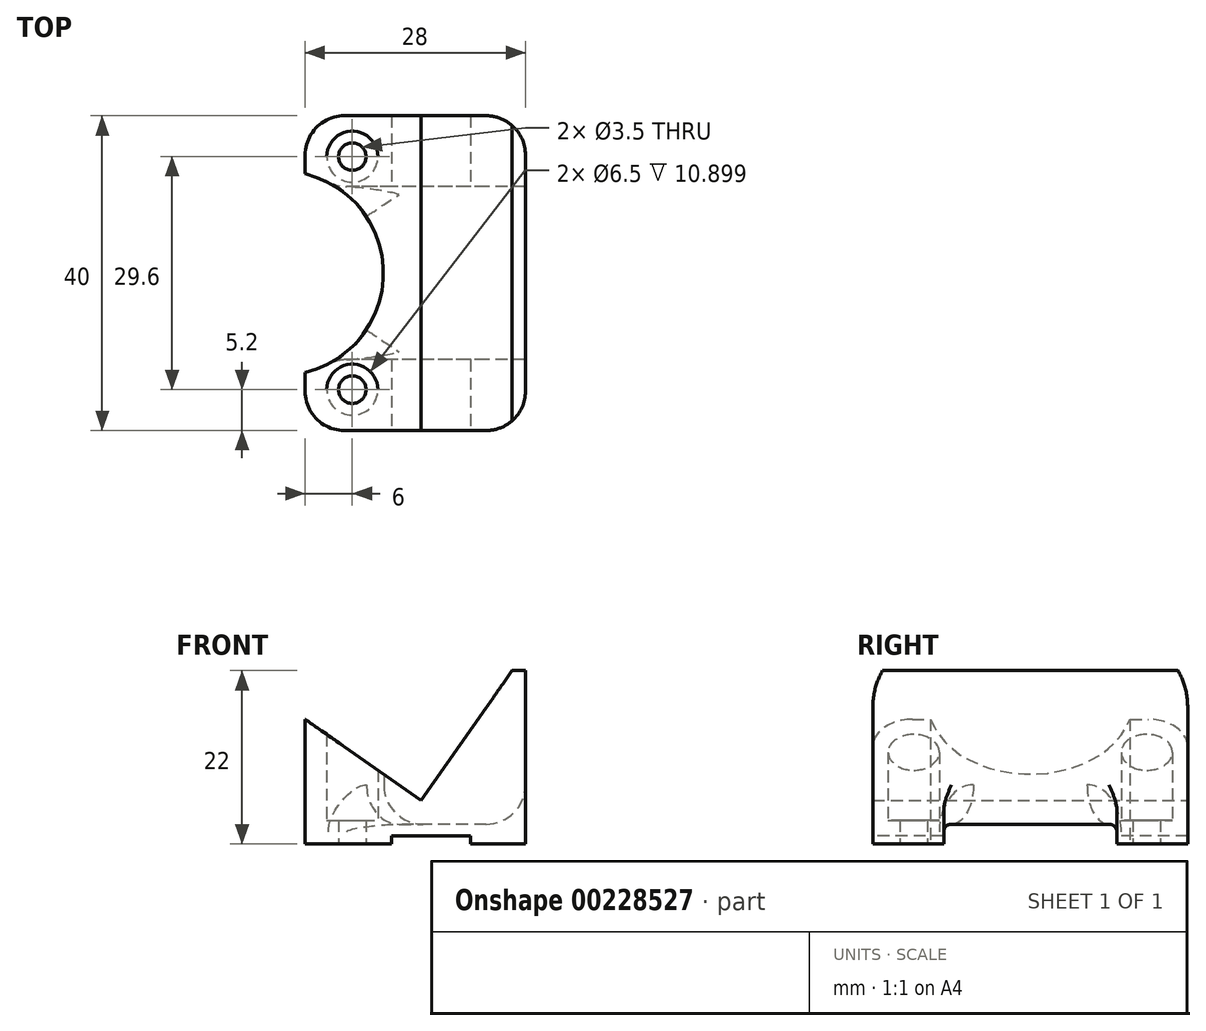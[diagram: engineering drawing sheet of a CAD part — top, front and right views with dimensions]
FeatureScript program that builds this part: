
annotation { "Feature Type Name" : "Feature", "Feature Type Description" : "" }
export const myFeature = defineFeature(function(context is Context, id is Id, definition is map)
    precondition{}
    {
        {
            var Q0;
            Q0=qCreatedBy(makeId("Front.planeOp"),FACE);
            var sketch = newSketch(context, id + "F0", { "sketchPlane" : qUnion([Q0])});
            skLineSegment(sketch, "E0.bottom", {"start": v(0, 0) * mm, "end": v(28, 0) * mm});
            skLineSegment(sketch, "E0.top", {"start": v(26.3, 22) * mm, "end": v(28, 22) * mm});
            skLineSegment(sketch, "E0.left", {"start": v(0, 0) * mm, "end": v(0, 15.82) * mm});
            skLineSegment(sketch, "E0.right", {"start": v(28, 0) * mm, "end": v(28, 22) * mm});
            skLineSegment(sketch, "E1", {"start": v(0, 15.82) * mm, "end": v(14.74, 5.5) * mm});
            skLineSegment(sketch, "E2", {"start": v(14.74, 5.5) * mm, "end": v(26.3, 22) * mm});
            skSolve(sketch);
        }
        {
            var Q0;
            Q0=qSketchRegion(id+"F0",true);
            extrude(context, id + "F1", {"entities" : qUnion([Q0]), "endBound" : BoundingType.SYMMETRIC, "depth" : 40 * mm});
        }
        {
            var Q0;
            Q0=makeQuery(id+"F1.opExtrude","SWEPT_FACE",FACE,{"disambiguationData":[OSD([sQuery(id+"F0.wireOp",EDGE,"E0.bottom")])]});
            var sketch = newSketch(context, id + "F2", { "sketchPlane" : qUnion([Q0])});
            skCircle(sketch, "E3", {"center": v(6, 14.8) * mm, "radius": 1.75 * mm});
            skCircle(sketch, "E4", {"center": v(6, -14.8) * mm, "radius": 1.75 * mm});
            skCircle(sketch, "E5", {"center": v(-3, 0) * mm, "radius": 13 * mm});
            skSolve(sketch);
        }
        {
            var Q0;
            Q0=qSketchRegion(id+"F2",true);
            extrude(context, id + "F3", {"entities" : qUnion([Q0]), "operationType" : NewBodyOperationType.REMOVE, "endBound" : BoundingType.THROUGH_ALL, "oppositeDirection" : true, "depth" : 25 * mm});
        }
        {
            var Q0;
            Q0=makeQuery(id+"F1.opExtrude","SWEPT_FACE",FACE,{"disambiguationData":[OSD([sQuery(id+"F0.wireOp",EDGE,"E0.left")])]});
            var sketch = newSketch(context, id + "F4", { "sketchPlane" : qUnion([Q0])});
            skLineSegment(sketch, "E6.bottom", {"start": v(-11, 2.5) * mm, "end": v(11, 2.5) * mm});
            skLineSegment(sketch, "E6.top", {"start": v(-11, 0) * mm, "end": v(11, 0) * mm});
            skLineSegment(sketch, "E6.left", {"start": v(-11, 2.5) * mm, "end": v(-11, 0) * mm});
            skLineSegment(sketch, "E6.right", {"start": v(11, 2.5) * mm, "end": v(11, 0) * mm});
            skSolve(sketch);
        }
        {
            var Q0;
            Q0=qSketchRegion(id+"F4",true);
            extrude(context, id + "F5", {"entities" : qUnion([Q0]), "operationType" : NewBodyOperationType.REMOVE, "endBound" : BoundingType.THROUGH_ALL, "oppositeDirection" : true, "depth" : 25 * mm});
        }
        {
            var Q0;
            Q0=makeQuery(id+"F5.boolean.opBoolean","INTERSECT",EDGE,{"derivedFrom":[makeQuery(id+"F1.opExtrude","SWEPT_FACE",FACE,{"disambiguationData":[OSD([sQuery(id+"F0.wireOp",EDGE,"E0.right")])]}),makeQuery(id+"F5.opExtrude","SWEPT_FACE",FACE,{"disambiguationData":[OSD([sQuery(id+"F4.wireOp",EDGE,"E6.bottom")])]})]});
            fillet(context, id + "F6", {"entities" : qUnion([Q0]), "radius" : 5 * mm, "tangentPropagation" : true, "allowEdgeOverflow" : false});
        }
        {
            var Q0;
            Q0=makeQuery(id+"F1.opExtrude","CAP_EDGE",EDGE,{"disambiguationData":[OSD([sQuery(id+"F0.wireOp",EDGE,"E0.left")])],"isStart":false});
            var Q1;
            Q1=makeQuery(id+"F1.opExtrude","CAP_EDGE",EDGE,{"disambiguationData":[OSD([sQuery(id+"F0.wireOp",EDGE,"E0.left")])],"isStart":true});
            fillet(context, id + "F7", {"entities" : qUnion([Q0, Q1]), "radius" : 5 * mm, "tangentPropagation" : true, "allowEdgeOverflow" : false});
        }
        {
            var Q0;
            Q0=makeQuery(id+"F5.boolean.opBoolean","COPY",EDGE,{"derivedFrom":makeQuery(id+"F5.opExtrude","SWEPT_EDGE",EDGE,{"disambiguationData":[OSD([sQuery(id+"F4.wireOp",EDGE,"E6.bottom"),sQuery(id+"F4.wireOp",EDGE,"E6.left")])]})});
            var Q1;
            Q1=makeQuery(id+"F5.boolean.opBoolean","COPY",EDGE,{"derivedFrom":makeQuery(id+"F5.opExtrude","SWEPT_EDGE",EDGE,{"disambiguationData":[OSD([sQuery(id+"F4.wireOp",EDGE,"E6.bottom"),sQuery(id+"F4.wireOp",EDGE,"E6.right")])]})});
            fillet(context, id + "F8", {"entities" : qUnion([Q0, Q1]), "radius" : 1 * mm, "tangentPropagation" : true, "allowEdgeOverflow" : false});
        }
        {
            var Q0;
            Q0=makeQuery(id+"F1.opExtrude","CAP_EDGE",EDGE,{"disambiguationData":[OSD([sQuery(id+"F0.wireOp",EDGE,"E0.right")])],"isStart":true});
            var Q1;
            Q1=makeQuery(id+"F1.opExtrude","CAP_EDGE",EDGE,{"disambiguationData":[OSD([sQuery(id+"F0.wireOp",EDGE,"E0.right")])],"isStart":false});
            fillet(context, id + "F9", {"entities" : qUnion([Q0, Q1]), "radius" : 5 * mm, "tangentPropagation" : true, "allowEdgeOverflow" : false});
        }
        {
            var Q0;
            {var subQ2=sQuery(id+"F0.wireOp",EDGE,"E0.bottom");Q0=makeQuery(id+"F5.boolean.opBoolean","SPLIT",FACE,{"disambiguationData":[TD([makeQuery(id+"F3.boolean.opBoolean","COPY",FACE,{"derivedFrom":makeQuery(id+"F3.opExtrude","SWEPT_FACE",FACE,{"disambiguationData":[OSD([sQuery(id+"F2.wireOp",EDGE,"E4")])]})})])],"derivedFrom":makeQuery(id+"F1.opExtrude","SWEPT_FACE",FACE,{"disambiguationData":[OSD([subQ2])]})});}
            var sketch = newSketch(context, id + "F10", { "sketchPlane" : qUnion([Q0])});
            skCircle(sketch, "E7", {"center": v(6, 14.8) * mm, "radius": 3.25 * mm});
            skCircle(sketch, "E8", {"center": v(6, -14.8) * mm, "radius": 3.25 * mm});
            skSolve(sketch);
        }
        {
            var Q0;
            Q0=qSketchRegion(id+"F10",true);
            extrude(context, id + "F11", {"entities" : qUnion([Q0]), "operationType" : NewBodyOperationType.REMOVE, "oppositeDirection" : true, "depth" : 25 * mm, "hasSecondDirection" : true, "secondDirectionOppositeDirection" : true, "secondDirectionDepth" : 3 * mm});
        }
        {
            var Q0;
            Q0=makeQuery(id+"F5.boolean.opBoolean","INTERSECT",EDGE,{"derivedFrom":[makeQuery(id+"F3.boolean.opBoolean","COPY",FACE,{"derivedFrom":makeQuery(id+"F3.opExtrude","SWEPT_FACE",FACE,{"disambiguationData":[OSD([sQuery(id+"F2.wireOp",EDGE,"E5")])]})}),makeQuery(id+"F5.opExtrude","SWEPT_FACE",FACE,{"disambiguationData":[OSD([sQuery(id+"F4.wireOp",EDGE,"E6.bottom")])]})]});
            fillet(context, id + "F12", {"entities" : qUnion([Q0]), "radius" : 5 * mm, "tangentPropagation" : true, "allowEdgeOverflow" : false});
        }
        {
            var Q0;
            Q0=makeQuery(id+"F1.opExtrude","CAP_FACE",FACE,{"disambiguationData":[OSD([sQuery(id+"F0.wireOp",EDGE,"E0.bottom"),sQuery(id+"F0.wireOp",EDGE,"E0.top"),sQuery(id+"F0.wireOp",EDGE,"E0.left"),sQuery(id+"F0.wireOp",EDGE,"E0.right"),sQuery(id+"F0.wireOp",EDGE,"E1"),sQuery(id+"F0.wireOp",EDGE,"E2")])],"isStart":false});
            var sketch = newSketch(context, id + "F13", { "sketchPlane" : qUnion([Q0])});
            skLineSegment(sketch, "E9.bottom", {"start": v(11, 0) * mm, "end": v(21, 0) * mm});
            skLineSegment(sketch, "E9.top", {"start": v(11, 1) * mm, "end": v(21, 1) * mm});
            skLineSegment(sketch, "E9.left", {"start": v(11, 0) * mm, "end": v(11, 1) * mm});
            skLineSegment(sketch, "E9.right", {"start": v(21, 0) * mm, "end": v(21, 1) * mm});
            skSolve(sketch);
        }
        {
            var Q0;
            Q0 = qSketchRegion(id + "F13", true);
            extrude(context, id + "F14", {"entities" : qUnion([Q0]), "operationType" : NewBodyOperationType.REMOVE, "endBound" : BoundingType.THROUGH_ALL, "oppositeDirection" : true, "depth" : 25 * mm});
        }
    });
